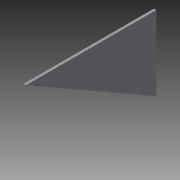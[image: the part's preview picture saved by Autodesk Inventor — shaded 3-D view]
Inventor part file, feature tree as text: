
AUTODESK INVENTOR PART (.ipt)
format: ipt  version: 2015 SP1 (Build 190203100, 203)  size: 67,584 bytes
history: native  units: in
note: dims shown in document units (in); Inventor stores cm internally (conversion verified against a paired STEP export)
features: extrude x1, sketch x1
ambient origin geometry x8: Origin, YZ Plane, XZ Plane, XY Plane, X Axis, Y Axis, Z Axis, Center Point
bodies: Solid1 (feature_tree)
feature tree (2):
  extrude  "Extrusion1"  Depth=6.75in
  sketch  "Sketch1"  dims[d0=3.875in d1=6.75in d2=0.125in d3=0.0in]
